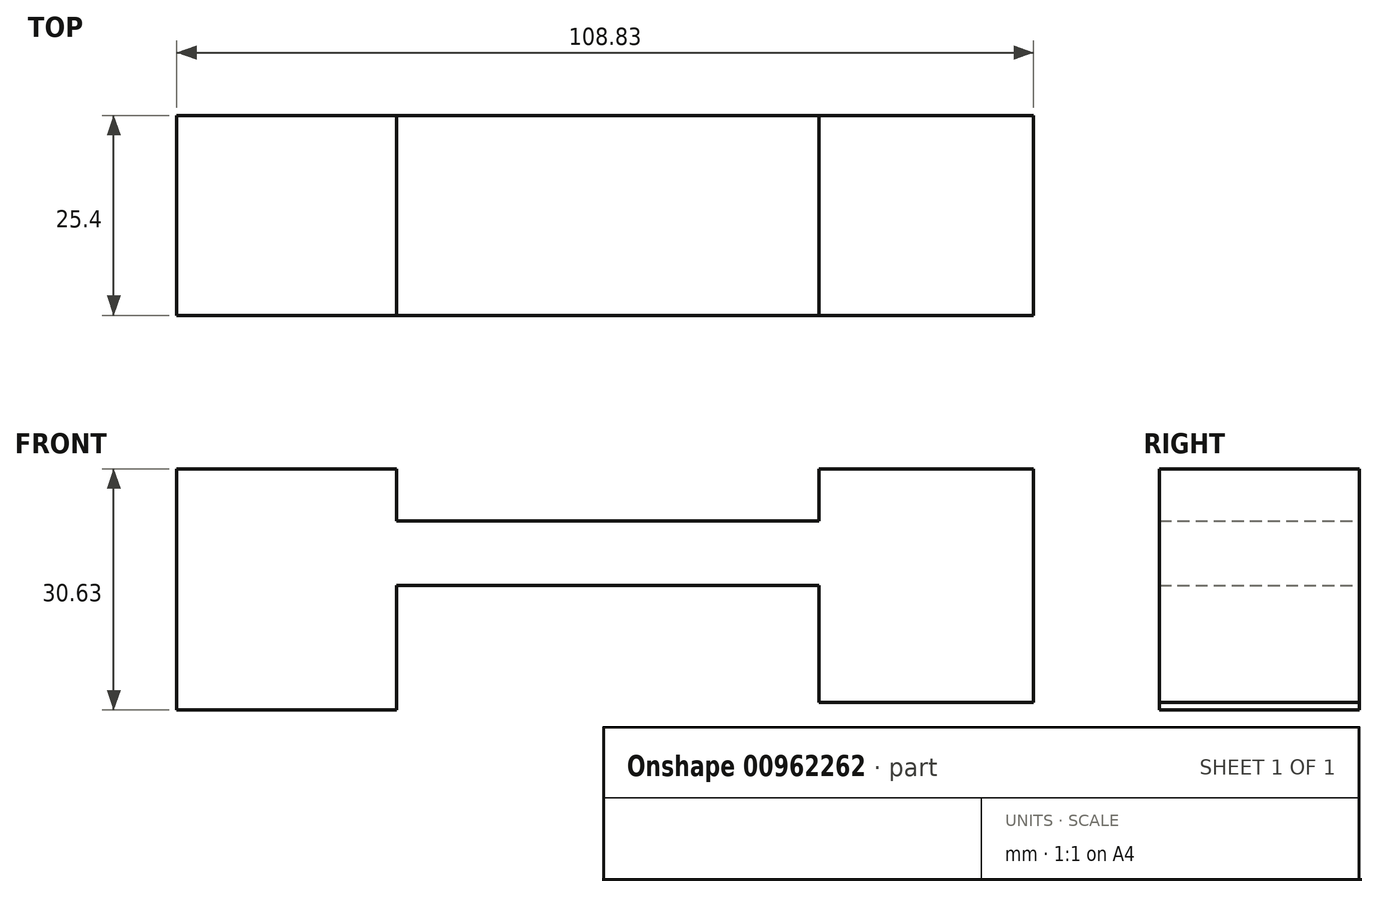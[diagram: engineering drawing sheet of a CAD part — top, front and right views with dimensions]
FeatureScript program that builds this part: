
annotation { "Feature Type Name" : "Feature", "Feature Type Description" : "" }
export const myFeature = defineFeature(function(context is Context, id is Id, definition is map)
    precondition{}
    {
        {
            var Q0;
            Q0=qCreatedBy(makeId("Front.planeOp"),FACE);
            var sketch = newSketch(context, id + "F0", { "sketchPlane" : qUnion([Q0])});
            skLineSegment(sketch, "E0.bottom", {"start": v(54.6, 0) * mm, "end": v(27.33, 0) * mm});
            skLineSegment(sketch, "E0.top", {"start": v(54.6, -29.63) * mm, "end": v(27.33, -29.63) * mm});
            skLineSegment(sketch, "E0.left", {"start": v(54.6, 0) * mm, "end": v(54.6, -29.63) * mm});
            skLineSegment(sketch, "E0.right", {"start": v(27.33, 0) * mm, "end": v(27.33, -29.63) * mm});
            skLineSegment(sketch, "E1.bottom", {"start": v(-54.23, 0) * mm, "end": v(-26.34, 0) * mm});
            skLineSegment(sketch, "E1.top", {"start": v(-54.23, -30.63) * mm, "end": v(-26.34, -30.63) * mm});
            skLineSegment(sketch, "E1.left", {"start": v(-54.23, 0) * mm, "end": v(-54.23, -30.63) * mm});
            skLineSegment(sketch, "E1.right", {"start": v(-26.34, 0) * mm, "end": v(-26.34, -30.63) * mm});
            skLineSegment(sketch, "E2.bottom", {"start": v(27.33, -14.82) * mm, "end": v(-26.34, -14.82) * mm});
            skLineSegment(sketch, "E2.top", {"start": v(27.33, -6.63) * mm, "end": v(-26.34, -6.63) * mm});
            skLineSegment(sketch, "E2.left", {"start": v(27.33, -14.82) * mm, "end": v(27.33, -6.63) * mm});
            skLineSegment(sketch, "E2.right", {"start": v(-26.34, -14.82) * mm, "end": v(-26.34, -6.63) * mm});
            skSolve(sketch);
        }
        {
            var Q0;
            {var subQ1=sQuery(id+"F0.wireOp",EDGE,"E0.bottom");Q0=makeQuery(id+"F0.imprint","IMPRINT",FACE,{"disambiguationData":[TD([[makeQuery(id+"F0.imprint","IMPRINT",EDGE,{"derivedFrom":subQ1}),1.0]])]});}
            var Q1;
            Q1 = qSketchRegion(id + "F0", true);
            var Q2;
            {var subQ1=sQuery(id+"F0.wireOp",EDGE,"E1.bottom");Q2=makeQuery(id+"F0.imprint","IMPRINT",FACE,{"disambiguationData":[TD([[makeQuery(id+"F0.imprint","IMPRINT",EDGE,{"derivedFrom":subQ1}),-1.0]])]});}
            extrude(context, id + "F1", {"entities" : qUnion([Q0, Q1, Q2]), "depth" : 25.4 * mm, "offsetDistance" : 25.4 * mm});
        }
    });
